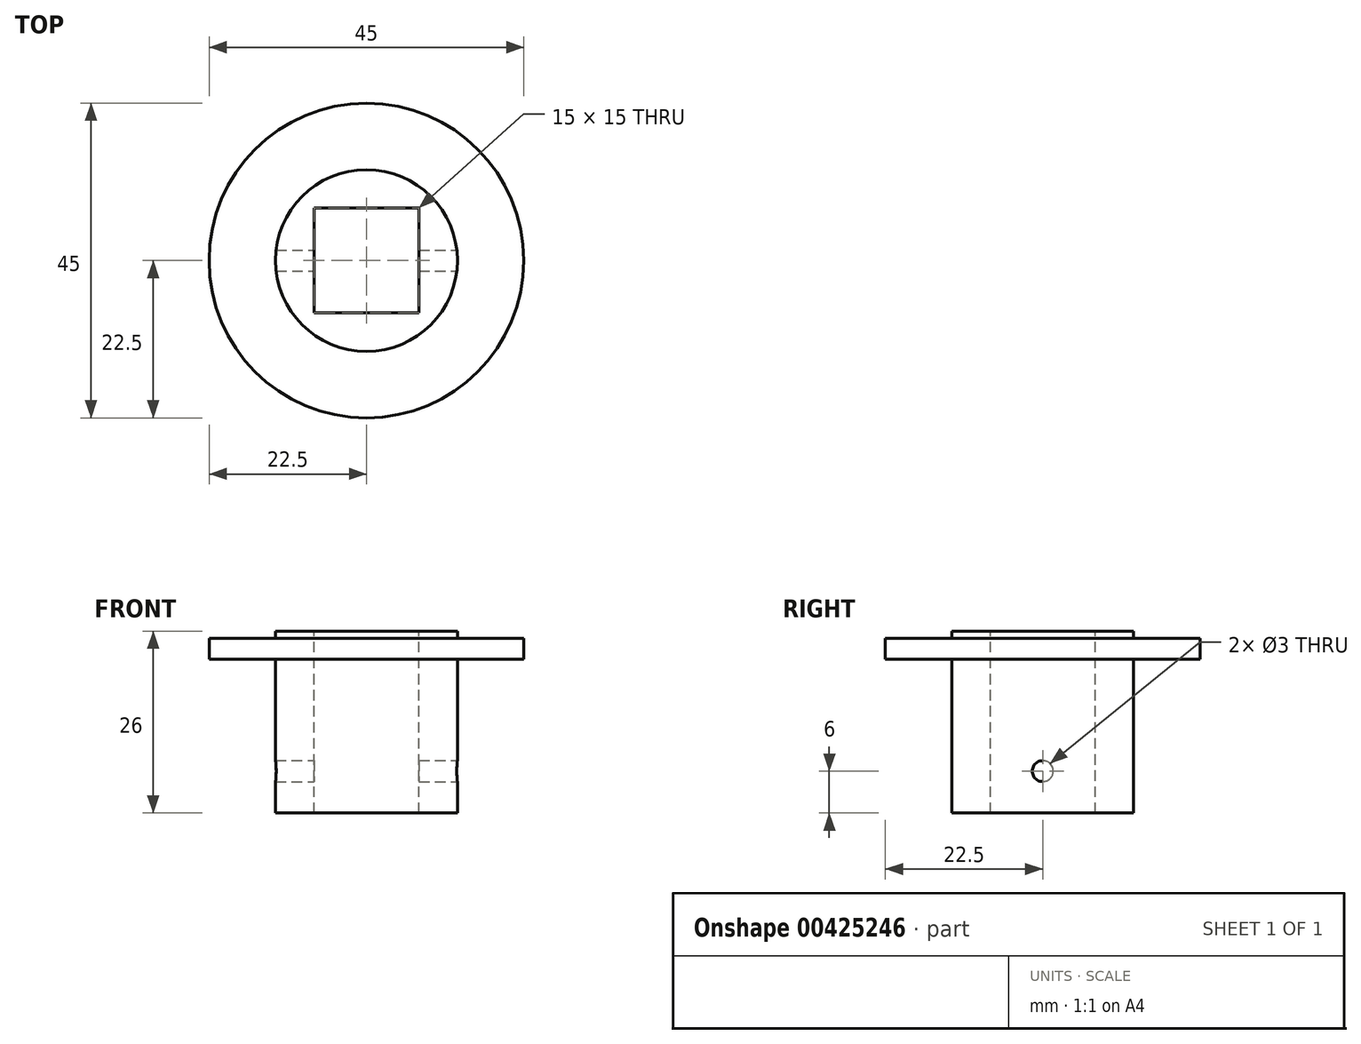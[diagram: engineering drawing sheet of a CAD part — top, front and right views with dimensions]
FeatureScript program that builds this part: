
annotation { "Feature Type Name" : "Feature", "Feature Type Description" : "" }
export const myFeature = defineFeature(function(context is Context, id is Id, definition is map)
    precondition{}
    {
        {
            var Q0;
            Q0=qCreatedBy(makeId("Top.planeOp"),FACE);
            var sketch = newSketch(context, id + "F0", { "sketchPlane" : qUnion([Q0])});
            skCircle(sketch, "E0", {"center": v(0, 0) * mm, "radius": 13 * mm});
            skSolve(sketch);
        }
        {
            var Q0;
            Q0=makeQuery(id+"F0.imprint","IMPRINT",FACE,{"disambiguationData":[TD([[makeQuery(id+"F0.imprint","IMPRINT",EDGE,{"derivedFrom":sQuery(id+"F0.wireOp",EDGE,"E0")}),1.0]])]});
            extrude(context, id + "F1", {"entities" : qUnion([Q0]), "endBound" : BoundingType.SYMMETRIC, "depth" : 26 * mm});
        }
        {
            var Q0;
            Q0=makeQuery(id+"F1.opExtrude","CAP_FACE",FACE,{"disambiguationData":[OSD([sQuery(id+"F0.wireOp",EDGE,"E0")])],"isStart":false});
            cPlane(context, id + "F2", {"entities" : qUnion([Q0]), "cplaneType" : CPlaneType.OFFSET, "offset" : 1 * mm, "oppositeDirection" : true, "width" : 150 * mm, "height" : 150 * mm});
        }
        {
            var Q0;
            Q0=qCreatedBy(id+"F2.planeOp",FACE);
            var sketch = newSketch(context, id + "F3", { "sketchPlane" : qUnion([Q0])});
            skCircle(sketch, "E1", {"center": v(0, 0) * mm, "radius": 22.5 * mm});
            skSolve(sketch);
        }
        {
            var Q0;
            Q0=makeQuery(id+"F3.imprint","IMPRINT",FACE,{"disambiguationData":[TD([[makeQuery(id+"F3.imprint","IMPRINT",EDGE,{"derivedFrom":sQuery(id+"F3.wireOp",EDGE,"E1")}),1.0]])]});
            extrude(context, id + "F4", {"entities" : qUnion([Q0]), "operationType" : NewBodyOperationType.ADD, "oppositeDirection" : true, "depth" : 3 * mm});
        }
        {
            var Q0;
            Q0=makeQuery(id+"F1.opExtrude","CAP_FACE",FACE,{"disambiguationData":[OSD([sQuery(id+"F0.wireOp",EDGE,"E0")])],"isStart":false});
            var sketch = newSketch(context, id + "F5", { "sketchPlane" : qUnion([Q0])});
            skLineSegment(sketch, "E2.bottom", {"start": v(7.5, 7.5) * mm, "end": v(-7.5, 7.5) * mm});
            skLineSegment(sketch, "E2.top", {"start": v(7.5, -7.5) * mm, "end": v(-7.5, -7.5) * mm});
            skLineSegment(sketch, "E2.left", {"start": v(7.5, 7.5) * mm, "end": v(7.5, -7.5) * mm});
            skLineSegment(sketch, "E2.right", {"start": v(-7.5, 7.5) * mm, "end": v(-7.5, -7.5) * mm});
            skPoint(sketch, "E2.middle", {"position": v(0, 0) * mm});
            skSolve(sketch);
        }
        {
            var Q0;
            Q0=makeQuery(id+"F5.imprint","IMPRINT",FACE,{"disambiguationData":[TD([[makeQuery(id+"F5.imprint","IMPRINT",EDGE,{"derivedFrom":sQuery(id+"F5.wireOp",EDGE,"E2.bottom")}),1.0]])]});
            extrude(context, id + "F6", {"entities" : qUnion([Q0]), "operationType" : NewBodyOperationType.REMOVE, "oppositeDirection" : true, "depth" : 58.6 * mm});
        }
        {
            var Q0;
            Q0=qCreatedBy(makeId("Right.planeOp"),FACE);
            var sketch = newSketch(context, id + "F7", { "sketchPlane" : qUnion([Q0])});
            skCircle(sketch, "E3", {"center": v(0, -7) * mm, "radius": 1.5 * mm});
            skSolve(sketch);
        }
        {
            var Q0;
            Q0=makeQuery(id+"F7.imprint","IMPRINT",FACE,{"disambiguationData":[TD([[makeQuery(id+"F7.imprint","IMPRINT",EDGE,{"derivedFrom":sQuery(id+"F7.wireOp",EDGE,"E3")}),1.0]])]});
            extrude(context, id + "F8", {"entities" : qUnion([Q0]), "operationType" : NewBodyOperationType.REMOVE, "endBound" : BoundingType.SYMMETRIC, "oppositeDirection" : true, "depth" : 50 * mm});
        }
    });
